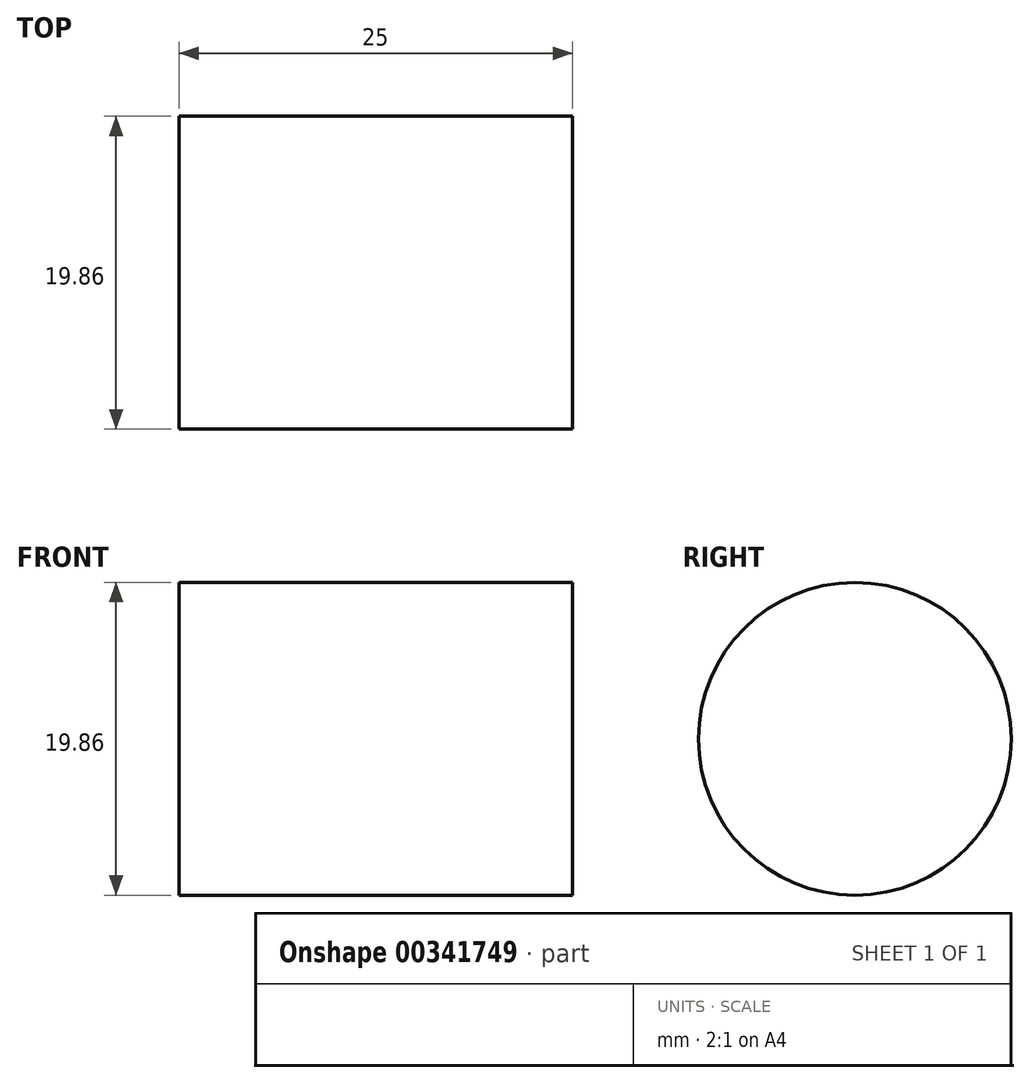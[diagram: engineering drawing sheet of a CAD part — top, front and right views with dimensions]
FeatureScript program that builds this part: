
annotation { "Feature Type Name" : "Feature", "Feature Type Description" : "" }
export const myFeature = defineFeature(function(context is Context, id is Id, definition is map)
    precondition{}
    {
        {
            var Q0;
            Q0=qCreatedBy(makeId("Right.planeOp"),FACE);
            var sketch = newSketch(context, id + "F0", { "sketchPlane" : qUnion([Q0])});
            skCircle(sketch, "E0", {"center": v(0, 0) * mm, "radius": 9.93 * mm});
            skSolve(sketch);
        }
        {
            var Q0;
            Q0 = qSketchRegion(id + "F0", true);
            extrude(context, id + "F1", {"entities" : qUnion([Q0]), "depth" : 25 * mm});
        }
    });
